# Revit family: Lighting_Fixture-Wall-Astro-Massa_350_LED
name_source: partatom
category: Lighting Fixtures
revit_build: Autodesk Revit 2014 (Build: 20130308_1515(x64)
units: mm (PartAtom-declared; Revit-internal decimal feet)

## types (1)
- 7394 Massa 350
    Apparent Load = 24 VA
    Assembly Code = D5020200
    Casing Material = Astro - Steel - White
    Class = 2
    Color Filter = 16777215
    Description = Wall Light
    Dimmable = No
    Dimming Lamp Color Temperature Shift = <None>
    Energy Efficiency Rating = A
    Height = 345 mm  [stored 1.13189 ft]
    IP Rating = IP44
    Lamp = LED
    Lamp included = Yes
    Length = 108.95 mm  [stored 0.357448 ft]
    Light Source Elevation = 1600 mm  [stored 5.24934 ft]
    Light Source From Wall = 45 mm  [stored 0.147638 ft]
    Luminaire Lamp Efficiency Rating = A
    Manufacturer = Astro Lighting Ltd, CM20 2DP
    Model = 7394 Massa 350
    Mountable on normally flammable surfaces = Yes
    Number of Poles = 1
    Photometric Web File = 7394 MASSA 350.ies
    Product Documentation = http://www.astrolighting.co.uk
    Suitable for bathroom zone = Zone 2, 3
    Tilt Angle = 0.00°
    Type Comments = -Includes integral LED driver
    URL = www.astrolighting.co.uk
    Voltage = 230 V
    Wattage Comments = 24w
    Weight = 1.51 kg
    Width = 345 mm  [stored 1.13189 ft]

note: [stored X ft] marks values corroborated as IEEE doubles in the binary element streams (Revit-internal decimal feet)

## geometry (parser evidence)
native form markers: Sweep x4
no freeform markers — native parametric forms only
